# Revit family: LO-200
name_source: partatom
category: Mechanical Equipment
revit_build: Autodesk Revit 2018 (Build: 20190510_1515(x64)
units: mm (PartAtom-declared; Revit-internal decimal feet)

## family parameters
Always vertical = Yes
Cut with Voids When Loaded = No
OmniClass Number = 23.75.00.00
OmniClass Title = Climate Control (HVAC)
Part Type = Normal
Room Calculation Point = No
Round Connector Dimension = Use Diameter
Shared = No
Work Plane-Based = No

## types (8) — shared parameters
Hz = 60
Phase = 3
URL = www.preferred-mfg.com
Volts = 208, 230, 460

## per-type parameters (varying)
- LO-201_50PSI: A=1' - 4 1/8"; B=0' - 8 1/2"; C=0' - 5 1/2"; D=1' - 8"; E=0' - 5 7/8"; F=1' - 6"; G=0' - 8 5/8"; GPH. Oil No.2 / No.4=305 / 337; H=0' - 7"; I=0' - 1"; J=0' - 2"; L=0' - 2"; LO-201=0' - 0"; LO-202=3' - 0"; LO-203=4' - 0"; LO-204=5' - 0"; LO-205=6' - 0"; LO-206=7' - 0"; LO-207=8' - 0"; LO-208=9' - 0"; Model LO-201=Yes; Model LO-202=No; Model LO-203=No; Model LO-204=No; Model LO-205=No; Model LO-206=No; Model LO-207=No; Model LO-208=No; Motor HP=1/2; Motor RPM=1140; PSI=50.00 psi; Weight (lbs.)=58.00 lbm
- LO-202_100PSI: A=1' - 4 3/4"; B=0' - 9 1/2"; C=0' - 5 1/2"; D=1' - 9 7/8"; E=0' - 6 3/8"; F=1' - 6"; G=0' - 9 5/8"; GPH. Oil No.2 / No.4=300 / 400; H=0' - 8"; I=0' - 1"; J=0' - 3 5/16"; L=0' - 3 5/16"; LO-201=2' - 0"; LO-202=0' - 0"; LO-203=4' - 0"; LO-204=5' - 0"; LO-205=6' - 0"; LO-206=7' - 0"; LO-207=8' - 0"; LO-208=9' - 0"; Model LO-201=No; Model LO-202=Yes; Model LO-203=No; Model LO-204=No; Model LO-205=No; Model LO-206=No; Model LO-207=No; Model LO-208=No; Motor HP=3/4; Motor RPM=1140; PSI=100.00 psi; Weight (lbs.)=77.00 lbm
- LO-203_50PSI: A=1' - 7 1/4"; B=0' - 10 1/2"; C=0' - 7 1/2"; D=2' - 0 3/16"; E=0' - 7 1/2"; F=1' - 8"; G=0' - 10 1/2"; GPH. Oil No.2 / No.4=757 / 875; H=0' - 10"; I=0' - 1 1/2"; J=0' - 3 1/16"; L=0' - 3 1/16"; LO-201=2' - 0"; LO-202=3' - 0"; LO-203=0' - 0"; LO-204=5' - 0"; LO-205=6' - 0"; LO-206=7' - 0"; LO-207=8' - 0"; LO-208=9' - 0"; Model LO-201=No; Model LO-202=No; Model LO-203=Yes; Model LO-204=No; Model LO-205=No; Model LO-206=No; Model LO-207=No; Model LO-208=No; Motor HP=3/4; Motor RPM=1140; PSI=50.00 psi; Weight (lbs.)=99.00 lbm
- LO-204_100PSI: A=1' - 8 3/4"; B=0' - 11 11/16"; C=0' - 7 1/2"; D=2' - 3 13/32"; E=0' - 7 7/8"; F=1' - 9"; G=0' - 11 1/2"; GPH. Oil No.2 / No.4=714 / 881; H=0' - 10"; I=0' - 1 1/2"; J=0' - 4 27/32"; L=0' - 4 27/32"; LO-201=2' - 0"; LO-202=3' - 0"; LO-203=4' - 0"; LO-204=0' - 0"; LO-205=6' - 0"; LO-206=7' - 0"; LO-207=8' - 0"; LO-208=9' - 0"; Model LO-201=No; Model LO-202=No; Model LO-203=No; Model LO-204=Yes; Model LO-205=No; Model LO-206=No; Model LO-207=No; Model LO-208=No; Motor HP=1-1/2; Motor RPM=1140; PSI=100.00 psi; Weight (lbs.)=120.00 lbm
- LO-205_50PSI: A=1' - 8 3/4"; B=0' - 11 11/16"; C=0' - 7 1/2"; D=2' - 3 7/16"; E=0' - 7 7/8"; F=1' - 9"; G=0' - 11 1/2"; GPH. Oil No.2 / No.4=1095 / 1277; H=0' - 10"; I=0' - 1 1/2"; J=0' - 4 27/32"; L=0' - 4 27/32"; LO-201=2' - 0"; LO-202=3' - 0"; LO-203=4' - 0"; LO-204=5' - 0"; LO-205=0' - 0"; LO-206=7' - 0"; LO-207=8' - 0"; LO-208=9' - 0"; Model LO-201=No; Model LO-202=No; Model LO-203=No; Model LO-204=No; Model LO-205=Yes; Model LO-206=No; Model LO-207=No; Model LO-208=No; Motor HP=1-1/2; Motor RPM=1165; PSI=50.00 psi; Weight (lbs.)=134.00 lbm
- LO-206_100PSI: A=1' - 8 11/16"; B=0' - 11 11/16"; C=0' - 7 1/2"; D=2' - 5"; E=0' - 7 7/8"; F=1' - 9"; G=1' - 1 3/8"; GPH. Oil No.2 / No.4=1005 / 1277; H=0' - 10"; I=0' - 1 1/2"; J=0' - 6 11/32"; L=0' - 6 11/32"; LO-201=2' - 0"; LO-202=3' - 0"; LO-203=4' - 0"; LO-204=5' - 0"; LO-205=6' - 0"; LO-206=0' - 0"; LO-207=8' - 0"; LO-208=9' - 0"; Model LO-201=No; Model LO-202=No; Model LO-203=No; Model LO-204=No; Model LO-205=No; Model LO-206=Yes; Model LO-207=No; Model LO-208=No; Motor HP=2; Motor RPM=1170; PSI=100.00 psi; Weight (lbs.)=142.00 lbm
- LO-207_50PSI: A=2' - 1"; B=0' - 11 11/16"; C=0' - 10"; D=2' - 9 7/16"; E=0' - 9 1/16"; F=2' - 2"; G=1' - 2 1/16"; GPH. Oil No.2 / No.4=1931 / 2185; H=0' - 10"; I=0' - 2 1/2"; J=0' - 6"; L=0' - 6"; LO-201=2' - 0"; LO-202=3' - 0"; LO-203=4' - 0"; LO-204=5' - 0"; LO-205=6' - 0"; LO-206=7' - 0"; LO-207=0' - 0"; LO-208=9' - 0"; Model LO-201=No; Model LO-202=No; Model LO-203=No; Model LO-204=No; Model LO-205=No; Model LO-206=No; Model LO-207=Yes; Model LO-208=No; Motor HP=2; Motor RPM=1170; PSI=50.00 psi; Weight (lbs.)=225.00 lbm
- LO-208_100PSI: A=2' - 3 1/4"; B=1' - 1 13/16"; C=0' - 10"; D=2' - 11"; E=0' - 9 1/2"; F=2' - 4"; G=1' - 3 3/8"; GPH. Oil No.2 / No.4=1745 / 2105; H=1' - 0"; I=0' - 2 1/2"; J=0' - 5 5/16"; L=0' - 5 5/16"; LO-201=2' - 0"; LO-202=3' - 0"; LO-203=4' - 0"; LO-204=5' - 0"; LO-205=6' - 0"; LO-206=7' - 0"; LO-207=8' - 0"; LO-208=0' - 0"; Model LO-201=No; Model LO-202=No; Model LO-203=No; Model LO-204=No; Model LO-205=No; Model LO-206=No; Model LO-207=No; Model LO-208=Yes; Motor HP=5; Motor RPM=1165; PSI=100.00 psi; Weight (lbs.)=290.00 lbm

## geometry (parser evidence)
native form markers: Sweep x3
no freeform markers — native parametric forms only
